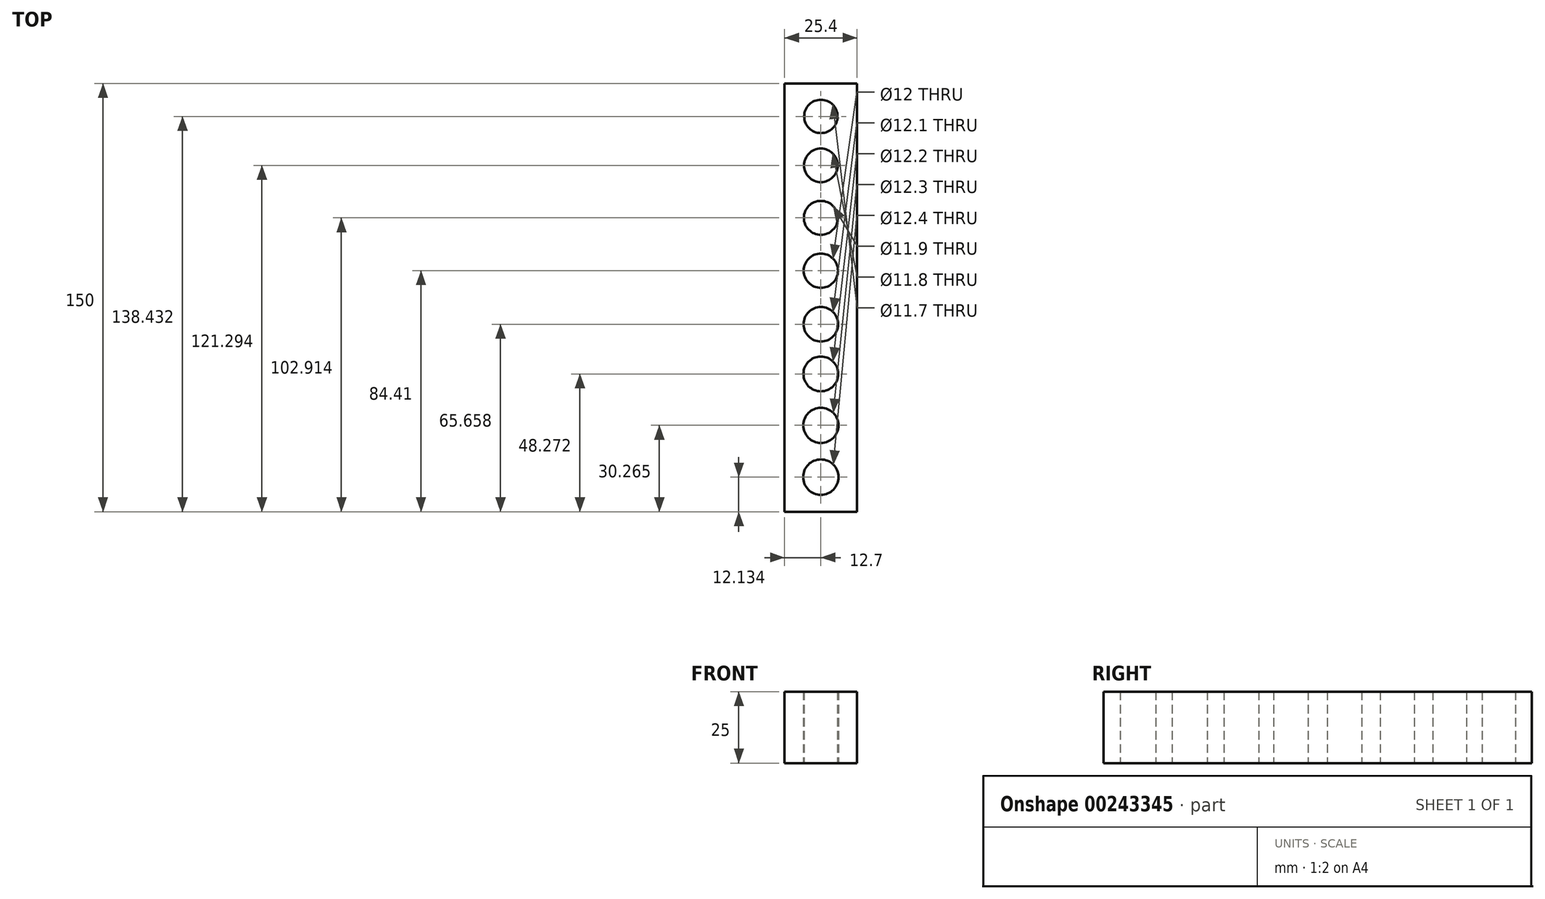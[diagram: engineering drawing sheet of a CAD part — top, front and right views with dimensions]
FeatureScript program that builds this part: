
annotation { "Feature Type Name" : "Feature", "Feature Type Description" : "" }
export const myFeature = defineFeature(function(context is Context, id is Id, definition is map)
    precondition{}
    {
        {
            var Q0;
            Q0=qCreatedBy(makeId("Top.planeOp"),FACE);
            var sketch = newSketch(context, id + "F0", { "sketchPlane" : qUnion([Q0])});
            skLineSegment(sketch, "E0.bottom", {"start": v(-12.7, 75) * mm, "end": v(12.7, 75) * mm});
            skLineSegment(sketch, "E0.top", {"start": v(-12.7, -75) * mm, "end": v(12.7, -75) * mm});
            skLineSegment(sketch, "E0.left", {"start": v(-12.7, 75) * mm, "end": v(-12.7, -75) * mm});
            skLineSegment(sketch, "E0.right", {"start": v(12.7, 75) * mm, "end": v(12.7, -75) * mm});
            skPoint(sketch, "E0.middle", {"position": v(0, 0) * mm});
            skCircle(sketch, "E1", {"center": v(0, 9.41) * mm, "radius": 6 * mm});
            skLineSegment(sketch, "E2", {"start": v(0, 75) * mm, "end": v(0, -75) * mm, "construction": true});
            skCircle(sketch, "E3", {"center": v(0, -9.34) * mm, "radius": 6.05 * mm});
            skCircle(sketch, "E4", {"center": v(0, -26.73) * mm, "radius": 6.1 * mm});
            skCircle(sketch, "E5", {"center": v(0, -44.73) * mm, "radius": 6.15 * mm});
            skCircle(sketch, "E6", {"center": v(0, -62.87) * mm, "radius": 6.2 * mm});
            skCircle(sketch, "E7", {"center": v(0, 27.91) * mm, "radius": 5.95 * mm});
            skCircle(sketch, "E8", {"center": v(0, 46.3) * mm, "radius": 5.9 * mm});
            skCircle(sketch, "E9", {"center": v(0, 63.43) * mm, "radius": 5.85 * mm});
            skSolve(sketch);
        }
        {
            var Q0;
            Q0 = qSketchRegion(id + "F0", true);
            extrude(context, id + "F1", {"entities" : qUnion([Q0]), "depth" : 25 * mm});
        }
    });
